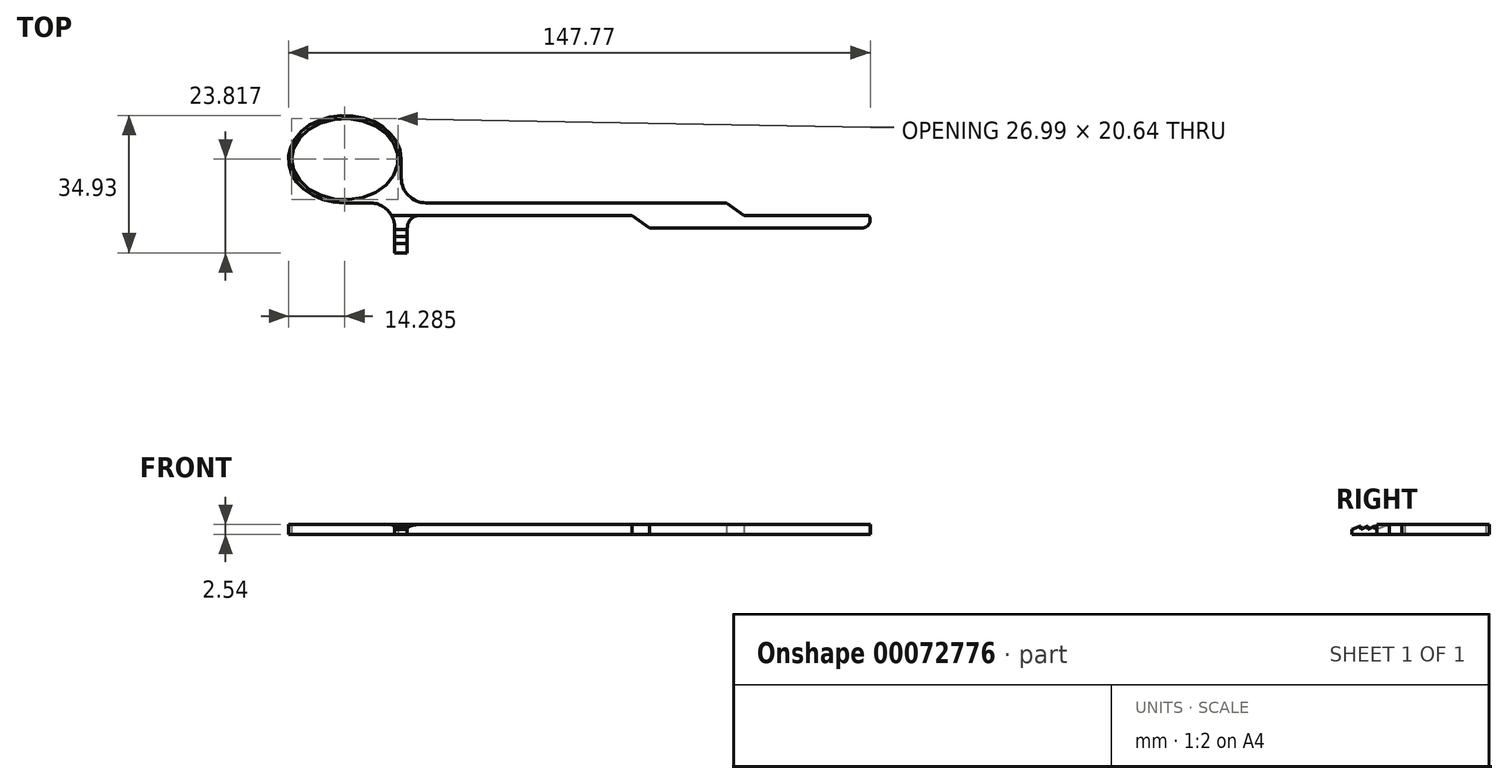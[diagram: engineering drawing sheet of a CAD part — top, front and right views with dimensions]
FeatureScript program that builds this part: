
annotation { "Feature Type Name" : "Feature", "Feature Type Description" : "" }
export const myFeature = defineFeature(function(context is Context, id is Id, definition is map)
    precondition{}
    {
        {
            var Q0;
            Q0=qCreatedBy(makeId("Top.planeOp"),FACE);
            var sketch = newSketch(context, id + "F0", { "sketchPlane" : qUnion([Q0])});
            skLineSegment(sketch, "E0", {"start": v(0, 0) * mm, "end": v(-53.98, 0) * mm});
            skLineSegment(sketch, "E1", {"start": v(-57.15, -3.18) * mm, "end": v(-57.15, -9.53) * mm});
            skLineSegment(sketch, "E2", {"start": v(-52.34, 3.18) * mm, "end": v(23.92, 3.18) * mm});
            skLineSegment(sketch, "E3", {"start": v(0, 0) * mm, "end": v(0, -3.17) * mm});
            skLineSegment(sketch, "E4", {"start": v(0, -3.17) * mm, "end": v(4.45, -3.17) * mm});
            skLineSegment(sketch, "E5", {"start": v(4.45, -3.18) * mm, "end": v(0, 0) * mm});
            skLineSegment(sketch, "E6", {"start": v(4.45, -3.18) * mm, "end": v(58.42, -3.17) * mm});
            skLineSegment(sketch, "E7", {"start": v(23.92, 3.18) * mm, "end": v(23.92, 0) * mm});
            skLineSegment(sketch, "E8", {"start": v(23.92, 0) * mm, "end": v(28.36, 0) * mm});
            skLineSegment(sketch, "E9", {"start": v(28.36, 0) * mm, "end": v(23.92, 3.18) * mm});
            skLineSegment(sketch, "E10", {"start": v(28.36, 0) * mm, "end": v(60.11, 0) * mm});
            skArc(sketch, "E11", {"start": v(58.42, -3.17) * mm, "mid": v(60.22, -2.1) * mm, "end": v(60.11, 0) * mm});
            skLineSegment(sketch, "E12", {"start": v(28.36, 0) * mm, "end": v(26.1, -3.18) * mm});
            skLineSegment(sketch, "E13", {"start": v(0, 3.18) * mm, "end": v(-1.27, 0) * mm});
            skLineSegment(sketch, "E14", {"start": v(-57.15, -9.53) * mm, "end": v(-60.33, -9.53) * mm});
            skLineSegment(sketch, "E15", {"start": v(-60.33, -9.53) * mm, "end": v(-60.33, -3.18) * mm});
            skLineSegment(sketch, "E16", {"start": v(-66.67, 3.17) * mm, "end": v(-73.03, 3.17) * mm});
            skLineSegment(sketch, "E17", {"start": v(-73.03, 3.17) * mm, "end": v(-73.03, 25.4) * mm});
            skEllipse(sketch, "E18", {"center": v(-73.03, 14.29) * mm, "majorRadius": 11.11 * mm, "minorRadius": 14.29 * mm, "majorAxis": v(0, 1)});
            skPoint(sketch, "E19.endSnap0", {"position": v(-58.74, 14.29) * mm});
            skLineSegment(sketch, "E20", {"start": v(-58.7, 9.46) * mm, "end": v(-58.74, 14.29) * mm});
            skArc(sketch, "E21.filletArc", {"start": v(-60.32, -3.18) * mm, "mid": v(-62.18, 1.32) * mm, "end": v(-66.67, 3.17) * mm});
            skArc(sketch, "E22.filletArc", {"start": v(-58.7, 9.46) * mm, "mid": v(-56.81, 5.01) * mm, "end": v(-52.34, 3.18) * mm});
            skEllipse(sketch, "E23", {"center": v(-73.03, 14.29) * mm, "majorRadius": 10.32 * mm, "minorRadius": 13.5 * mm, "majorAxis": v(0, 1)});
            skArc(sketch, "E24.filletArc", {"start": v(-53.98, 0) * mm, "mid": v(-56.22, -0.93) * mm, "end": v(-57.15, -3.18) * mm});
            skSolve(sketch);
        }
        {
            var Q0;
            {var subQ0=sQuery(id+"F0.wireOp",EDGE,"DGPuSRCI-eGpj-kUr9-CLdF-BAg5E6106GaB");Q0=makeQuery(id+"F0.imprint","IMPRINT",FACE,{"disambiguationData":[TD([[makeQuery(id+"F0.imprint","IMPRINT",EDGE,{"derivedFrom":subQ0}),1.0]])]});}
            var Q1;
            {var subQ5=sQuery(id+"F0.wireOp",EDGE,"wSrZLpTD-TIs4-zcTP-NB4d-SKE6weNMGa0Q");Q1=makeQuery(id+"F0.imprint","IMPRINT",FACE,{"disambiguationData":[TD([[makeQuery(id+"F0.imprint","IMPRINT",EDGE,{"derivedFrom":subQ5}),-1.0]])]});}
            var Q2;
            {var subQ0=sQuery(id+"F0.wireOp",EDGE,"wSrZLpTD-TIs4-zcTP-NB4d-SKE6weNMGa0Q");Q2=makeQuery(id+"F0.imprint","IMPRINT",FACE,{"disambiguationData":[TD([[makeQuery(id+"F0.imprint","IMPRINT",EDGE,{"derivedFrom":subQ0}),1.0]])]});}
            var Q3;
            Q3=makeQuery(id+"F0.imprint","IMPRINT",FACE,{"disambiguationData":[TD([[makeQuery(id+"F0.imprint","IMPRINT",EDGE,{"derivedFrom":sQuery(id+"F0.wireOp",EDGE,"E10")}),-1.0]])]});
            var Q4;
            {var subQ1=sQuery(id+"F0.wireOp",EDGE,"E5");Q4=makeQuery(id+"F0.imprint","IMPRINT",FACE,{"disambiguationData":[TD([[makeQuery(id+"F0.imprint","IMPRINT",EDGE,{"derivedFrom":subQ1}),-1.0]])]});}
            var Q5;
            Q5=makeQuery(id+"F0.imprint","IMPRINT",FACE,{"disambiguationData":[TD([[makeQuery(id+"F0.imprint","IMPRINT",EDGE,{"derivedFrom":sQuery(id+"F0.wireOp",EDGE,"E7")}),1.0]])]});
            var Q6;
            {var subQ5=sQuery(id+"F0.wireOp",EDGE,"jsiKynNP-CTXm-Abzb-5jRY-FCptraazA1bC");Q6=makeQuery(id+"F0.imprint","IMPRINT",FACE,{"disambiguationData":[TD([[makeQuery(id+"F0.imprint","IMPRINT",EDGE,{"derivedFrom":subQ5}),-1.0]])]});}
            var Q7;
            {var subQ0=sQuery(id+"F0.wireOp",EDGE,"JKMu2kUw-y11I-2PMK-oWUd-3fX4LaI0biQn");Q7=makeQuery(id+"F0.imprint","IMPRINT",FACE,{"disambiguationData":[TD([[makeQuery(id+"F0.imprint","IMPRINT",EDGE,{"derivedFrom":subQ0}),-1.0]])]});}
            var Q8;
            {var subQ0=sQuery(id+"F0.wireOp",EDGE,"E17");Q8=makeQuery(id+"F0.imprint","IMPRINT",FACE,{"disambiguationData":[TD([[makeQuery(id+"F0.imprint","IMPRINT",EDGE,{"derivedFrom":subQ0}),-1.0]])]});}
            var Q9;
            {var subQ0=sQuery(id+"F0.wireOp",EDGE,"E17");Q9=makeQuery(id+"F0.imprint","IMPRINT",FACE,{"disambiguationData":[TD([[makeQuery(id+"F0.imprint","IMPRINT",EDGE,{"derivedFrom":subQ0}),1.0]])]});}
            var Q10;
            {var subQ6=sQuery(id+"F0.wireOp",EDGE,"E1");Q10=makeQuery(id+"F0.imprint","IMPRINT",FACE,{"disambiguationData":[TD([[makeQuery(id+"F0.imprint","IMPRINT",EDGE,{"derivedFrom":subQ6}),-1.0]])]});}
            extrude(context, id + "F1", {"entities" : qUnion([Q0, Q1, Q2, Q3, Q4, Q5, Q6, Q7, Q8, Q9, Q10]), "depth" : 1.27 * mm, "hasSecondDirection" : true, "secondDirectionOppositeDirection" : true, "secondDirectionDepth" : 1.27 * mm});
        }
        {
            var Q0;
            Q0=makeQuery(id+"F1.opExtrude","SWEPT_FACE",FACE,{"disambiguationData":[OSD([sQuery(id+"F0.wireOp",EDGE,"E15")])]});
            var sketch = newSketch(context, id + "F2", { "sketchPlane" : qUnion([Q0])});
            skLineSegment(sketch, "E25", {"start": v(0, 0) * mm, "end": v(0, 1.27) * mm});
            skLineSegment(sketch, "E26", {"start": v(0, 1.27) * mm, "end": v(3.6, 0) * mm});
            skPoint(sketch, "E26.endSnap0", {"position": v(3.18, 0) * mm});
            skLineSegment(sketch, "E27", {"start": v(3.6, 0) * mm, "end": v(3.6, 0.95) * mm});
            skLineSegment(sketch, "E28", {"start": v(3.6, 0.95) * mm, "end": v(5.39, 0) * mm});
            skLineSegment(sketch, "E29", {"start": v(5.39, 0) * mm, "end": v(5.39, 0.95) * mm});
            skLineSegment(sketch, "E30", {"start": v(5.39, 0.95) * mm, "end": v(7.18, 0) * mm});
            skLineSegment(sketch, "E31", {"start": v(7.18, 0) * mm, "end": v(7.18, 0.95) * mm});
            skLineSegment(sketch, "E32", {"start": v(7.18, 0.95) * mm, "end": v(9.53, 0) * mm});
            skLineSegment(sketch, "E33", {"start": v(0, 1.27) * mm, "end": v(9.53, 1.27) * mm});
            skLineSegment(sketch, "E34", {"start": v(9.53, 1.27) * mm, "end": v(9.53, 0) * mm});
            skSolve(sketch);
        }
        {
            var Q0;
            {var subQ0=sQuery(id+"F2.wireOp",EDGE,"E27");Q0=makeQuery(id+"F2.imprint","IMPRINT",FACE,{"disambiguationData":[TD([[makeQuery(id+"F2.imprint","IMPRINT",EDGE,{"derivedFrom":subQ0}),1.0]])]});}
            var Q1;
            {var subQ0=sQuery(id+"F2.wireOp",EDGE,"E33");Q1=makeQuery(id+"F2.imprint","IMPRINT",FACE,{"disambiguationData":[TD([[makeQuery(id+"F2.imprint","IMPRINT",EDGE,{"derivedFrom":subQ0}),-1.0]])]});}
            extrude(context, id + "F3", {"entities" : qUnion([Q0, Q1]), "operationType" : NewBodyOperationType.REMOVE, "endBound" : BoundingType.UP_TO_NEXT, "oppositeDirection" : true, "depth" : 25.4 * mm});
        }
        {
            var Q0;
            Q0=makeQuery(id+"F3.boolean.opBoolean","COPY",FACE,{"derivedFrom":makeQuery(id+"F3.opExtrude","CAP_FACE",FACE,{"disambiguationData":[OSD([sQuery(id+"F2.wireOp",EDGE,"E26"),sQuery(id+"F2.wireOp",EDGE,"E27"),sQuery(id+"F2.wireOp",EDGE,"E28"),sQuery(id+"F2.wireOp",EDGE,"E29"),sQuery(id+"F2.wireOp",EDGE,"E30"),sQuery(id+"F2.wireOp",EDGE,"E31"),sQuery(id+"F2.wireOp",EDGE,"E32"),sQuery(id+"F2.wireOp",EDGE,"E33"),sQuery(id+"F2.wireOp",EDGE,"E34")])],"isStart":true})});
            extrude(context, id + "F4", {"entities" : qUnion([Q0]), "operationType" : NewBodyOperationType.REMOVE, "endBound" : BoundingType.THROUGH_ALL, "oppositeDirection" : true, "depth" : 25.4 * mm});
        }
    });
